# Revit family: Shower-Showerhead-KOHLER-Real_Rain-K-76728
name_source: partatom
category: Plumbing Fixtures
revit_build: Autodesk Revit 2015 (Build: 20140606_1530(x64)
units: mm (PartAtom-declared; Revit-internal decimal feet)

## types (1)
- 0-White
    ADA Compliant = Yes
    Assembly Code = D2010700
    Date Modified = 09/08/2017
    Default Elevation = 0"
    Description = Real Rain overhead panel
    Finish = Kohler-Silicone-0-White
    Flow Rate = 2 GPM
    HW Connection = Yes
    Height = 4 21/32"
    Inlet Connector = Inlet Connection
    Length = 19 1/2"
    Manufacturer = Kohler
    MasterFormat 1995 = 15410
    MasterFormat 2004 = 22.41.23
    Material = Silicone Panel
    Model = K-76728-0
    Outlet Connector = Outlet Connection
    Pressure = 45.00 psi
    Product Documentation Link = http://www.us.kohler.com
    Product Name = Real Rain
    Product Page URL = http://www.us.kohler.com
    Type = 0
    URL = http://www.us.kohler.com
    Waste Connection = Yes
    Width = 19 1/2"

## geometry (parser evidence)
native form markers: Blend x8, Sweep x5
no freeform markers — native parametric forms only
